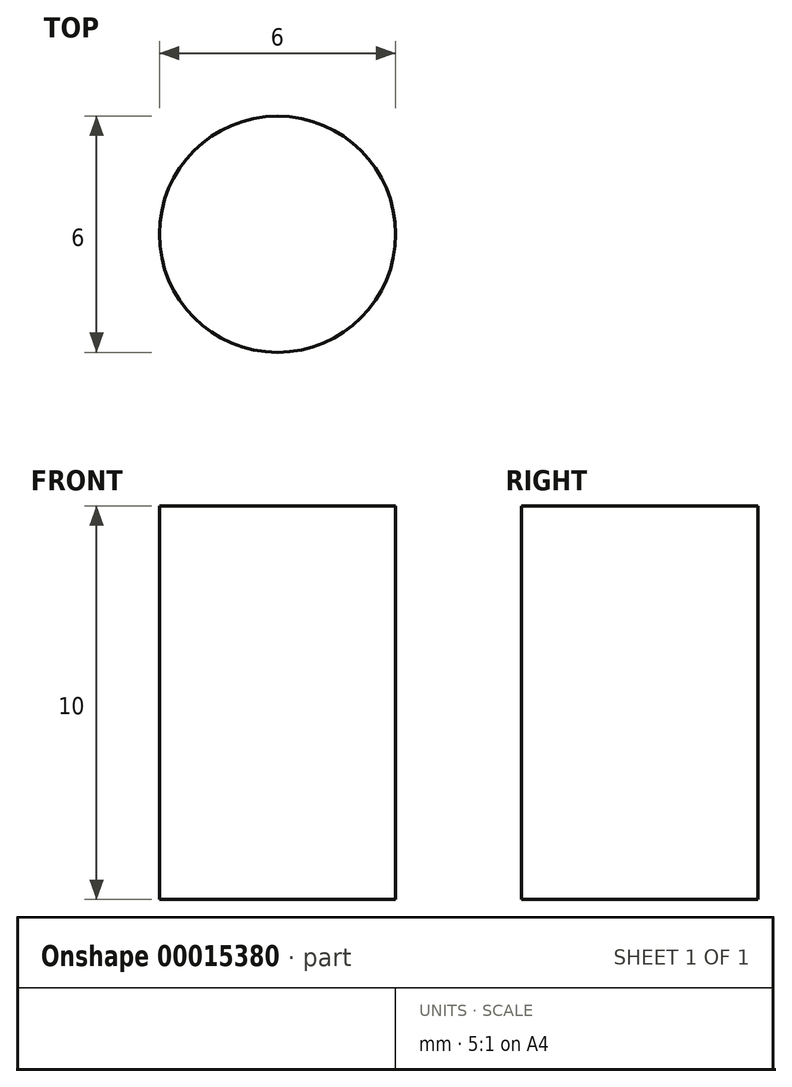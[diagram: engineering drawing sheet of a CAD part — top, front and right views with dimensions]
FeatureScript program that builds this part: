
annotation { "Feature Type Name" : "Feature", "Feature Type Description" : "" }
export const myFeature = defineFeature(function(context is Context, id is Id, definition is map)
    precondition{}
    {
        {
            var Q0;
            Q0=qCreatedBy(makeId("Top.planeOp"),FACE);
            var sketch = newSketch(context, id + "F0", { "sketchPlane" : qUnion([Q0])});
            skCircle(sketch, "E0", {"center": v(0, 0) * mm, "radius": 3 * mm});
            skSolve(sketch);
        }
        {
            var Q0;
            Q0=qSketchRegion(id+"F0",true);
            extrude(context, id + "F1", {"entities" : qUnion([Q0]), "depth" : 10 * mm});
        }
    });
